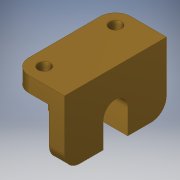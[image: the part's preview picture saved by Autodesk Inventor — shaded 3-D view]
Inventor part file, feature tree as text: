
AUTODESK INVENTOR PART (.ipt)
format: ipt  version: 2019 (Build 230136000, 136)  size: 189,952 bytes
history: native  units: mm
features: extrude x7, sketch x7, projected_geometry x2, chamfer x1, fillet x1
ambient origin geometry x8: Origin, YZ Plane, XZ Plane, XY Plane, X Axis, Y Axis, Z Axis, Center Point
bodies: Solid1 (feature_tree)
feature tree (18):
  extrude  "Extrusion1"  Depth=100.0mm
  extrude  "Extrusion2"  Depth=24.0mm
  extrude  "Extrusion3"  Depth=65.0mm TaperAngle=0.0deg
  extrude  "Extrusion4"  Depth=30.0mm
  extrude  "Extrusion5"  Depth=50.0mm TaperAngle=0.0deg
  extrude  "Extrusion6"  Depth=40.0mm
  chamfer  "Chamfer1"  Distance=4.0mm
  fillet  "Fillet1"  Radius=10.0mm
  extrude  "Extrusion7"  Depth=15.0mm
  sketch  "Sketch1"  dims[d0=50.0mm d1=100.0mm]
  sketch  "Sketch2"  dims[d2=65.0mm d3=0.0mm d5=24.0mm]
  sketch  "Sketch3"  dims[d6=65.0mm d7=0.0mm d8=65.0mm d9=0.0mm]
  projected_geometry  "Projected Loop1"
  sketch  "Sketch4"  dims[d10=35.0mm d11=30.0mm]
  sketch  "Sketch5"  dims[d12=30.0mm d13=50.0mm d14=0.0mm]
  projected_geometry  "Projected Loop2"
  sketch  "Sketch6"  dims[d15=40.0mm d16=40.0mm d17=4.0mm d18=0.0mm d19=10.0mm]
  sketch  "Sketch7"  dims[d20=15.0mm d21=15.0mm d22=4.0mm d23=0.0mm d24=15.0mm d25=2.0mm d26=45.0deg d27=15.0mm d28=12.0mm d29=12.0mm d30=15.0mm d31=15.0mm d32=15.0mm d33=15.0mm d34=4.0mm d35=0.0mm]
